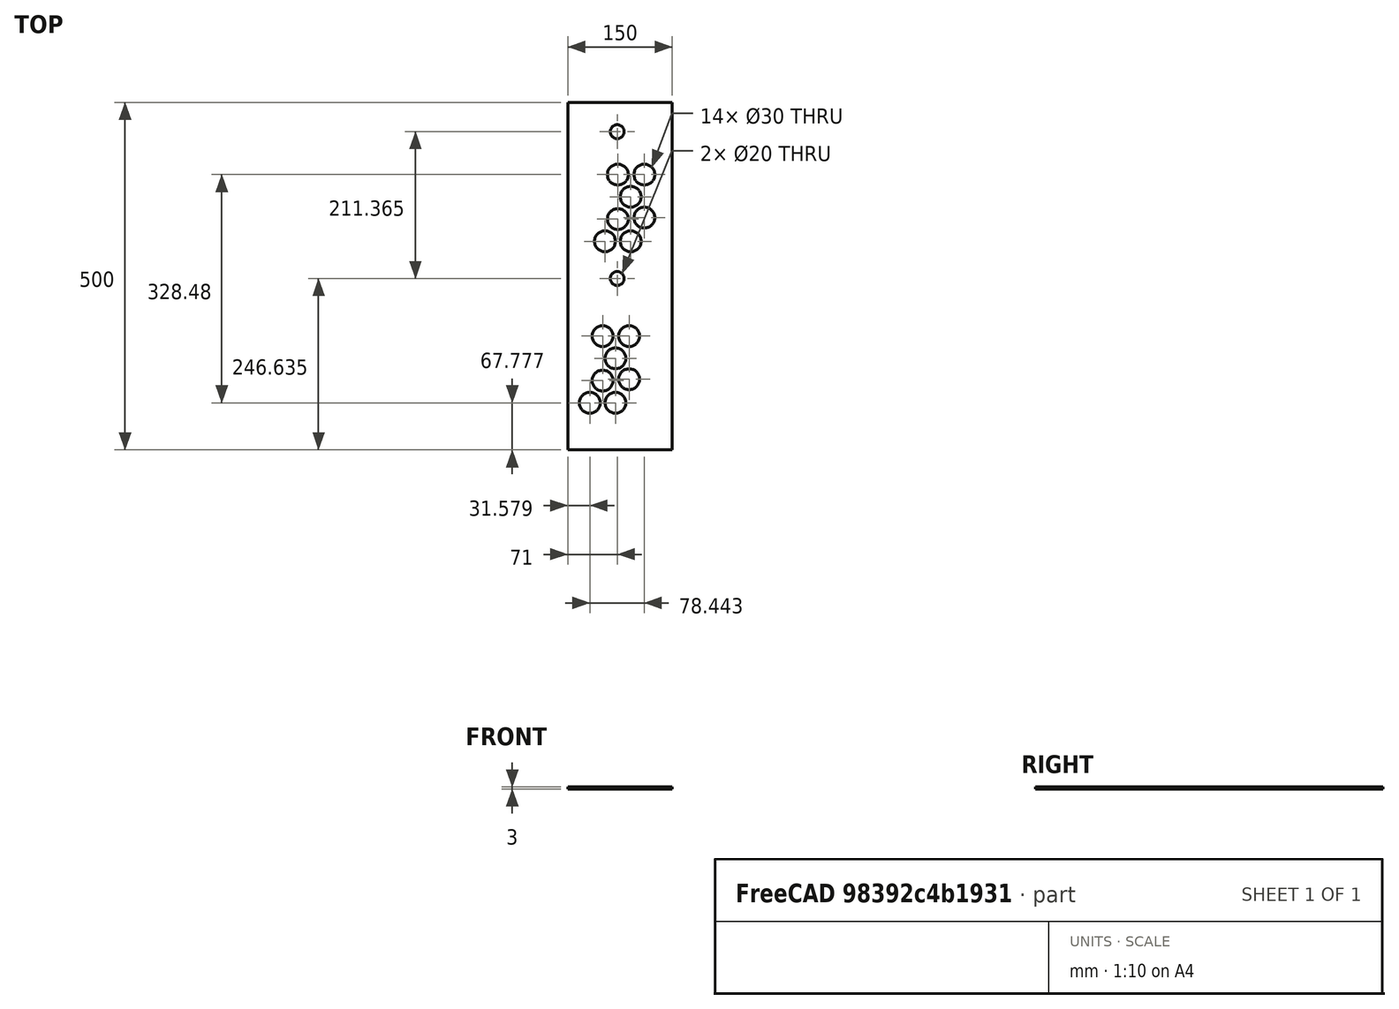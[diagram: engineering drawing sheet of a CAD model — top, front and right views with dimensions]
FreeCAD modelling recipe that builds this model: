
FCSTD DOCUMENT  (FreeCAD 0.18R14555 (Git shallow))
Label: 1001_keyboard_500_3_Duo
License: All rights reserved
LicenseURL: http://en.wikipedia.org/wiki/All_rights_reserved
objects: Sketcher::SketchObject×2, PartDesign::Pad×1, PartDesign::Pocket×1, PartDesign::Body×1, TechDraw::DrawSVGTemplate×1, TechDraw::DrawViewPart×1, TechDraw::DrawViewDimension×1, TechDraw::DrawPage×1, Spreadsheet::Sheet×1
note: 7 computed .brp shape members not serialized (recipe doc carries the construction recipe); baked Part::Feature solids carry a one-line shape summary decoded from their .brp

FEATURE [Sketcher::SketchObject] Sketch
  MapMode = 5
  Support = -> [XY_Plane]
  expr: Constraints[6] = xls.k_d
  expr: Constraints[5] = xls.k_w
  sketch-geometry (5):
    g0: LineSegment StartX=0 StartY=500 StartZ=0 EndX=150 EndY=500 EndZ=0
    g1: LineSegment StartX=150 StartY=500 StartZ=0 EndX=150 EndY=0 EndZ=0
    g2: LineSegment StartX=150 StartY=0 StartZ=0 EndX=0 EndY=0 EndZ=0
    g3: LineSegment StartX=0 StartY=0 StartZ=0 EndX=0 EndY=250 EndZ=0
    g4: LineSegment StartX=0 StartY=250 StartZ=0 EndX=0 EndY=500 EndZ=0
  constraints (14):
    c: Coincident(g0,g1)
    c: Coincident(g1,g2)
    c: Horizontal(g0)
    c: Horizontal(g2)
    c: Vertical(g1)
    c: DistanceY(g1,g1) = 500
    c: DistanceX(g0,g0) = 150
    c: Coincident(g3,g2)
    c: Coincident(g4,g0)
    c: Equal(g3,g4)
    c: Vertical(g4)
    c: Vertical(g3)
    c: Coincident(g3,g4)
    c: Coincident(g2,g-1)
FEATURE [PartDesign::Pad] Pad
  Length = 3
  Length2 = 100
  Profile = -> Sketch
  Type = 0
  expr: Length = xls.k_t_0
FEATURE [Sketcher::SketchObject] Sketch001
  ExternalGeometry = -> [Pad]
  MapMode = 5
  Placement = pos=(0,0,3) rot=(0,0,1;0rad)
  Support = -> [Pad]
  sketch-geometry (66):
    g0: LineSegment [constr] StartX=68.5295 StartY=67.7773 StartZ=0 EndX=68.5295 EndY=99.7773 EndZ=0
    g1: LineSegment [constr] StartX=68.5295 StartY=99.7773 StartZ=0 EndX=68.5295 EndY=131.777 EndZ=0
    g2: LineSegment [constr] StartX=68.5295 StartY=131.777 StartZ=0 EndX=68.5295 EndY=163.777 EndZ=0
    g3: LineSegment [constr] StartX=68.5295 StartY=131.777 StartZ=0 EndX=50.0543 EndY=163.777 EndZ=0
    g4: LineSegment [constr] StartX=68.5295 StartY=131.777 StartZ=0 EndX=50.0543 EndY=99.7773 EndZ=0
    g5: LineSegment [constr] StartX=50.0543 StartY=99.7773 StartZ=0 EndX=31.5791 EndY=67.7773 EndZ=0
    g6: LineSegment [constr] StartX=31.5791 StartY=67.7773 StartZ=0 EndX=68.5295 EndY=67.7773 EndZ=0
    g7: LineSegment [constr] StartX=50.0543 StartY=99.7773 StartZ=0 EndX=68.5295 EndY=99.7773 EndZ=0
    g8: LineSegment [constr] StartX=50.0543 StartY=163.777 StartZ=0 EndX=68.5295 EndY=163.777 EndZ=0
    g9: Circle CenterX=31.5791 CenterY=67.7773 CenterZ=0 NormalX=0 NormalY=0 NormalZ=1 AngleXU=0 Radius=15
    g10: Circle CenterX=50.0543 CenterY=99.7773 CenterZ=0 NormalX=0 NormalY=0 NormalZ=1 AngleXU=0 Radius=15
    g11: Circle CenterX=68.5295 CenterY=131.777 CenterZ=0 NormalX=0 NormalY=0 NormalZ=1 AngleXU=0 Radius=15
    g12: Circle CenterX=50.0543 CenterY=163.777 CenterZ=0 NormalX=0 NormalY=0 NormalZ=1 AngleXU=0 Radius=15
    g13: Circle CenterX=71 CenterY=246.635 CenterZ=0 NormalX=0 NormalY=0 NormalZ=1 AngleXU=0 Radius=10
    g14: LineSegment [constr] StartX=0 StartY=12 StartZ=0 EndX=136.275 EndY=12 EndZ=0
    g15: LineSegment [constr] StartX=136.275 StartY=12 StartZ=0 EndX=136.275 EndY=0 EndZ=0
    g16: LineSegment [constr] StartX=136.275 StartY=0 StartZ=0 EndX=0 EndY=0 EndZ=0
    g17: LineSegment [constr] StartX=0 StartY=0 StartZ=0 EndX=0 EndY=12 EndZ=0
    g18: LineSegment [constr] StartX=30 StartY=276.635 StartZ=0 EndX=112 EndY=276.635 EndZ=0
    g19: LineSegment [constr] StartX=112 StartY=276.635 StartZ=0 EndX=112 EndY=216.635 EndZ=0
    g20: LineSegment [constr] StartX=112 StartY=216.635 StartZ=0 EndX=30 EndY=216.635 EndZ=0
    g21: LineSegment [constr] StartX=30 StartY=216.635 StartZ=0 EndX=30 EndY=276.635 EndZ=0
    g22: LineSegment [constr] StartX=30 StartY=216.635 StartZ=0 EndX=71 EndY=246.635 EndZ=0
    g23: LineSegment [constr] StartX=71 StartY=246.635 StartZ=0 EndX=30 EndY=276.635 EndZ=0
    g24: LineSegment [constr] StartX=71 StartY=246.635 StartZ=0 EndX=112 EndY=216.635 EndZ=0
    g25: Circle CenterX=68.5295 CenterY=67.7773 CenterZ=0 NormalX=0 NormalY=0 NormalZ=1 AngleXU=0 Radius=15
    g26: Circle CenterX=88.1594 CenterY=101.777 CenterZ=0 NormalX=0 NormalY=0 NormalZ=1 AngleXU=0 Radius=15
    g27: LineSegment [constr] StartX=68.5295 StartY=67.7773 StartZ=0 EndX=88.1594 EndY=101.777 EndZ=0
    g28: LineSegment [constr] StartX=88.1594 StartY=101.777 StartZ=0 EndX=88.1594 EndY=163.777 EndZ=0
    g29: LineSegment [constr] StartX=88.1594 StartY=163.777 StartZ=0 EndX=68.5295 EndY=163.777 EndZ=0
    g30: Circle CenterX=88.1594 CenterY=163.777 CenterZ=0 NormalX=0 NormalY=0 NormalZ=1 AngleXU=0 Radius=15
    g31: LineSegment [constr] StartX=90.3919 StartY=300.257 StartZ=0 EndX=90.3919 EndY=332.257 EndZ=0
    g32: LineSegment [constr] StartX=90.3919 StartY=332.257 StartZ=0 EndX=90.3919 EndY=364.257 EndZ=0
    g33: LineSegment [constr] StartX=90.3919 StartY=364.257 StartZ=0 EndX=90.3919 EndY=396.257 EndZ=0
    g34: LineSegment [constr] StartX=90.3919 StartY=364.257 StartZ=0 EndX=71.9167 EndY=396.257 EndZ=0
    g35: LineSegment [constr] StartX=90.3919 StartY=364.257 StartZ=0 EndX=71.9167 EndY=332.257 EndZ=0
    g36: LineSegment [constr] StartX=71.9167 StartY=332.257 StartZ=0 EndX=53.4415 EndY=300.257 EndZ=0
    g37: LineSegment [constr] StartX=53.4415 StartY=300.257 StartZ=0 EndX=90.3919 EndY=300.257 EndZ=0
    g38: LineSegment [constr] StartX=71.9167 StartY=332.257 StartZ=0 EndX=90.3919 EndY=332.257 EndZ=0
    g39: LineSegment [constr] StartX=71.9167 StartY=396.257 StartZ=0 EndX=90.3919 EndY=396.257 EndZ=0
    g40: Circle CenterX=53.4415 CenterY=300.257 CenterZ=0 NormalX=0 NormalY=0 NormalZ=1 AngleXU=0 Radius=15
    g41: Circle CenterX=71.9167 CenterY=332.257 CenterZ=0 NormalX=0 NormalY=0 NormalZ=1 AngleXU=0 Radius=15
    g42: Circle CenterX=90.3919 CenterY=364.257 CenterZ=0 NormalX=0 NormalY=0 NormalZ=1 AngleXU=0 Radius=15
    g43: Circle CenterX=71.9167 CenterY=396.257 CenterZ=0 NormalX=0 NormalY=0 NormalZ=1 AngleXU=0 Radius=15
    g44: Circle CenterX=71 CenterY=458 CenterZ=0 NormalX=0 NormalY=0 NormalZ=1 AngleXU=0 Radius=10
    g45: LineSegment [constr] StartX=30 StartY=488 StartZ=0 EndX=112 EndY=488 EndZ=0
    g46: LineSegment [constr] StartX=112 StartY=488 StartZ=0 EndX=112 EndY=428 EndZ=0
    g47: LineSegment [constr] StartX=112 StartY=428 StartZ=0 EndX=30 EndY=428 EndZ=0
    g48: LineSegment [constr] StartX=30 StartY=428 StartZ=0 EndX=30 EndY=488 EndZ=0
    g49: LineSegment [constr] StartX=30 StartY=428 StartZ=0 EndX=71 EndY=458 EndZ=0
    g50: LineSegment [constr] StartX=71 StartY=458 StartZ=0 EndX=30 EndY=488 EndZ=0
    g51: LineSegment [constr] StartX=71 StartY=458 StartZ=0 EndX=112 EndY=428 EndZ=0
    g52: Circle CenterX=90.3919 CenterY=300.257 CenterZ=0 NormalX=0 NormalY=0 NormalZ=1 AngleXU=0 Radius=15
    g53: Circle CenterX=110.022 CenterY=334.257 CenterZ=0 NormalX=0 NormalY=0 NormalZ=1 AngleXU=0 Radius=15
    g54: LineSegment [constr] StartX=90.3919 StartY=300.257 StartZ=0 EndX=110.022 EndY=334.257 EndZ=0
    g55: LineSegment [constr] StartX=110.022 StartY=334.257 StartZ=0 EndX=110.022 EndY=396.257 EndZ=0
    g56: LineSegment [constr] StartX=110.022 StartY=396.257 StartZ=0 EndX=90.3919 EndY=396.257 EndZ=0
    g57: Circle CenterX=110.022 CenterY=396.257 CenterZ=0 NormalX=0 NormalY=0 NormalZ=1 AngleXU=0 Radius=15
    g58: LineSegment [constr] StartX=112 StartY=276.635 StartZ=0 EndX=168.795 EndY=276.635 EndZ=0
    g59: LineSegment [constr] StartX=168.795 StartY=276.635 StartZ=0 EndX=168.795 EndY=488 EndZ=0
    g60: LineSegment [constr] StartX=112 StartY=488 StartZ=0 EndX=168.795 EndY=488 EndZ=0
    g61: LineSegment [constr] StartX=150 StartY=500 StartZ=0 EndX=169.192 EndY=500 EndZ=0
    g62: LineSegment [constr] StartX=169.192 StartY=500 StartZ=0 EndX=168.795 EndY=488 EndZ=0
    g63: LineSegment [constr] StartX=30 StartY=276.635 StartZ=0 EndX=30 EndY=428 EndZ=0
    g64: GeomPoint X=112 Y=276.635 Z=0
    g65: LineSegment [constr] StartX=30 StartY=488 StartZ=0 EndX=0 EndY=488 EndZ=0
  constraints (166):
    c: Vertical(g0)
    c: Coincident(g2,g1)
    c: Vertical(g2)
    c: Vertical(g1)
    c: Coincident(g0,g1)
    c: Equal(g0,g1)
    c: Equal(g1,g2)
    c: DistanceY(g0,g0) = 32
    c: Coincident(g3,g1)
    c: Coincident(g4,g1)
    c: Coincident(g5,g4)
    c: Coincident(g6,g5)
    c: Coincident(g6,g0)
    c: Horizontal(g6)
    c: Coincident(g8,g3)
    c: Coincident(g8,g2)
    c: Horizontal(g8)
    c: Parallel(g4,g5)
    c: Coincident(g7,g4)
    c: Horizontal(g7)
    c: Coincident(g7,g0)
    c: Equal(g7,g8)
    c: Angle(g4,g1) = 0.523599
    c: Equal(g0,g1)
    c: Equal(g1,g2)
    c: Equal(g7,g8)
    c: Coincident(g9,g5)
    c: Coincident(g10,g4)
    c: Coincident(g11,g1)
    c: Coincident(g12,g3)
    c: Equal(g12,g11)
    c: Equal(g11,g10)
    c: Equal(g10,g9)
    c: Radius(g13) = 10
    c: Radius(g12) = 15
    c: Coincident(g14,g15)
    c: Coincident(g15,g16)
    c: Coincident(g16,g17)
    c: Coincident(g17,g14)
    c: Horizontal(g14)
    c: Horizontal(g16)
    c: Vertical(g15)
    c: Vertical(g17)
    c: DistanceY(g17,g17) = 12
    c: Coincident(g18,g19)
    c: Coincident(g19,g20)
    c: Coincident(g20,g21)
    c: Coincident(g21,g18)
    c: Horizontal(g18)
    c: Horizontal(g20)
    c: Vertical(g19)
    c: Vertical(g21)
    c: PointOnObject(g16,g-2)
    c: PointOnObject(g16,g-3)
    c: Coincident(g22,g20)
    c: Coincident(g23,g22)
    c: Coincident(g23,g18)
    c: Coincident(g24,g22)
    c: Coincident(g24,g19)
    c: Parallel(g24,g23)
    c: Equal(g24,g23)
    c: DistanceY(g21,g21) = 60
    c: DistanceX(g18,g18) = 82
    c: Coincident(g13,g22)
    c: Equal(g26,g25)
    c: Radius(g25) = 15
    c: Coincident(g27,g25)
    c: Coincident(g27,g26)
    c: DistanceY(g27,g27) = 34
    c: Angle(g27,g25) = 0.523599
    c: Coincident(g25,g0)
    c: Parallel(g27,g5)
    c: Coincident(g28,g26)
    c: Vertical(g28)
    c: Coincident(g29,g28)
    c: Coincident(g29,g2)
    c: Horizontal(g29)
    c: Coincident(g30,g28)
    c: Equal(g30,g12)
    c: Vertical(g31)
    c: Coincident(g33,g32)
    c: Vertical(g33)
    c: Vertical(g32)
    c: Coincident(g31,g32)
    c: Equal(g31,g32)
    c: Equal(g32,g33)
    c: Equal(g0,g31) = 32
    c: Coincident(g34,g32)
    c: Coincident(g35,g32)
    c: Coincident(g36,g35)
    c: Coincident(g37,g36)
    c: Coincident(g37,g31)
    c: Horizontal(g37)
    c: Coincident(g39,g34)
    c: Coincident(g39,g33)
    c: Horizontal(g39)
    c: Parallel(g35,g36)
    c: Coincident(g38,g35)
    c: Horizontal(g38)
    c: Coincident(g38,g31)
    c: Equal(g38,g39)
    c: Angle(g35,g32) = 0.523599
    c: Equal(g31,g32)
    c: Equal(g32,g33)
    c: Equal(g38,g39)
    c: Coincident(g40,g36)
    c: Coincident(g41,g35)
    c: Coincident(g42,g32)
    c: Coincident(g43,g34)
    c: Equal(g43,g42)
    c: Equal(g42,g41)
    c: Equal(g41,g40)
    c: Equal(g13,g44) = 10
    c: Equal(g12,g43) = 15
    c: Coincident(g45,g46)
    c: Coincident(g46,g47)
    c: Coincident(g47,g48)
    c: Coincident(g48,g45)
    c: Horizontal(g45)
    c: Horizontal(g47)
    c: Vertical(g46)
    c: Vertical(g48)
    c: Coincident(g49,g47)
    c: Coincident(g50,g49)
    c: Coincident(g50,g45)
    c: Coincident(g51,g49)
    c: Coincident(g51,g46)
    c: Parallel(g51,g50)
    c: Equal(g51,g50)
    c: Equal(g21,g48) = 40
    c: Equal(g18,g45) = 82
    c: Coincident(g44,g49)
    c: Equal(g53,g52)
    c: Equal(g25,g52) = 15
    c: Coincident(g54,g52)
    c: Coincident(g54,g53)
    c: Equal(g27,g54) = 34
    c: Angle(g54,g52) = 0.523599
    c: Coincident(g52,g31)
    c: Parallel(g54,g36)
    c: Coincident(g55,g53)
    c: Vertical(g55)
    c: Coincident(g56,g55)
    c: Coincident(g56,g33)
    c: Horizontal(g56)
    c: Coincident(g57,g55)
    c: Equal(g57,g43)
    c: Coincident(g60,g45)
    c: Coincident(g60,g59)
    c: Horizontal(g60)
    c: Coincident(g61,g-5)
    c: Horizontal(g61)
    c: Coincident(g62,g61)
    c: Coincident(g62,g59)
    c: DistanceY(g62,g62) = 12
    c: Coincident(g63,g18)
    c: Coincident(g63,g47)
    c: Vertical(g63)
    c: Coincident(g64,g58)
    c: Coincident(g18,g64)
    c: Coincident(g65,g45)
    c: PointOnObject(g65,g-2)
    c: Horizontal(g65)
    c: DistanceX(g65,g65) = 30
    c: Coincident(g58,g59)
    c: Horizontal(g58)
FEATURE [PartDesign::Pocket] Pocket
  BaseFeature = -> Pad
  Length = 5
  Length2 = 100
  Profile = -> Sketch001
  Type = 1
FEATURE [PartDesign::Body] Body
  Group = -> [Sketch,Pad,Sketch001,Pocket]
  Origin = -> Origin
  Tip = -> Pocket
FEATURE [TechDraw::DrawSVGTemplate] Template
  EditableTexts = AuthorName=AUTHOR NAME; CheckDate=CHECK DATE; CreationDate=CREATION DATE; DrawingNumber=NUMBER; FC-Scale=SCALE; FC-Title=TITLE; SheetNumber=SHEET; Subtitle=SUBTITLE; SupervisorName=SUPERVISOR NAME; Weight=WEIGHT
  Height = 297
  Orientation = 1
  Width = 420
FEATURE [TechDraw::DrawViewPart] View
  CoarseView = false
  Direction = (0,0,1)
  Focus = 100
  HardHidden = false
  IsoCount = 0
  IsoHidden = false
  IsoVisible = false
  LockPosition = false
  Perspective = false
  Rotation = -90
  ScaleType = 0
  SeamHidden = false
  SeamVisible = false
  SmoothHidden = false
  SmoothVisible = false
  Source = -> [Pocket]
  X = 210
  Y = 148.5
FEATURE [TechDraw::DrawViewDimension] Dimension
  Arbitrary = false
  FormatSpec = %.2f
  LockPosition = false
  MeasureType = 1
  OverTolerance = 0
  References2D = -> [View]
  Rotation = 0
  ScaleType = 0
  Type = 1
  UnderTolerance = 0
  X = 5.19444
  Y = 91.6667
FEATURE [TechDraw::DrawPage] Page
  KeepUpdated = true
  ProjectionType = 0
  Template = -> Template
  Views = -> [View,Dimension]
FEATURE [Spreadsheet::Sheet] Spreadsheet  label="xls"
  cells = B3=KEABOPARD; B4=Thickness; C4=k_t_0; D4(k_t_0)=3; E4=mm; F4=Note:; G4=Plexi is 3mm; B5=Width; C5=k_w; D5(k_w)=500; E5=mm; B6=Deapth; C6=k_d; D6(k_d)=150; E6=mm
